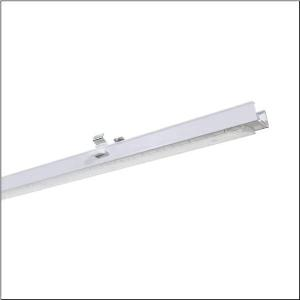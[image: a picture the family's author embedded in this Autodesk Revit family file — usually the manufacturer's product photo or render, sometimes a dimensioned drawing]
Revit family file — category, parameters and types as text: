
# Revit family: trunking_flex_31_51re12mb68b
name_source: partatom
category: Lighting Fixtures
units: mm (PartAtom-declared; Revit-internal decimal feet)

## family parameters
Cut with Voids When Loaded = No
Host = Face
Light Source = No
Part Type = Normal
Room Calculation Point = No
Round Connector Dimension = Use Diameter
Shared = No

## types (1)
- --- (1 x LED, 8000 lm, 50 W, 6500K)
    Apparent Load = 50 VA
    CIE Flux Codes = 65 91 98 99 100
    Color Rendering = 80
    Color Temperature = 6500K
    Default Elevation = 1800 mm
    Description = Trunking Flex 31, luminaire insert, of extruded aluminium section, coated, traffic white (RAL 9016), length: 1.472mm, width: 91mm, height: 53mm, LED rated luminous flux: 8.000lm, light colour: 865, control gear: ON/OFF Multilumen, with system connector: socket, mains connection: 220..240V, AC, 50/60Hz, rated input power: 50W, luminous flux adjustable on luminaire in four steps (4130/5610/6850/8000lm), connected load according to luminous flux setting (25/34/42/50W), primary light control with lens, of plastic, primary optical cover: cover, of PMMA, light emission: direct distribution, protection rating (complete): IP20, insulation class (complete): insulation class I (protective earthing), certification: CE, UKCA, impact resistance: IK02, permissible ambient temperature for indoor applications: -20..+40°C, packaging unit: 1 piece
    Height = 58 mm
    Lamp = 1 x LED
    Lamp Light Flux = 8000 lm
    Lamp Power = 50 W
    Lamp count = 1
    Length = 1472 mm
    Luminous efficacy = 160 lm/W
    Manufacturer = Siteco
    ModVariant = No
    Model = 51RE12MB68B
    Mounting Place = Ceiling
    Mounting Type = Pendant
    Number of Poles = 1
    OnlyDefault = Yes
    Power Factor = 1
    Product Name = Trunking Flex 31
    Product group = luminaire insert
    ProductGroupID = 901
    Protection Class = Protection class I
    Protection Degree = IP 20
    RLX_Detail_Level = 1
    RLX_Emergency_Light_Flux = 0 lm
    RLX_Emergency_Type = 0
    RLX_Emergency_Type_DB = No
    RlxData = <blob elided: 20329 chars, md5=4f85f993>
    Socket = socket
    Standby Power = 0 W
    System Light Flux = 8000 lm
    System Power = 50 W
    Type Comments = factory setting: luminous flux: 100 % | (ON | ON) | 300 mA
    Type Image = l_1266702.jpg
    URL = http://relux.com
    VarID = @adj_018609
    Voltage = 0 V
    Weight = 0.00 kg
    Width = 65 mm

## geometry (parser evidence)
native form markers: Blend x4, Sweep x10
no freeform markers — native parametric forms only
